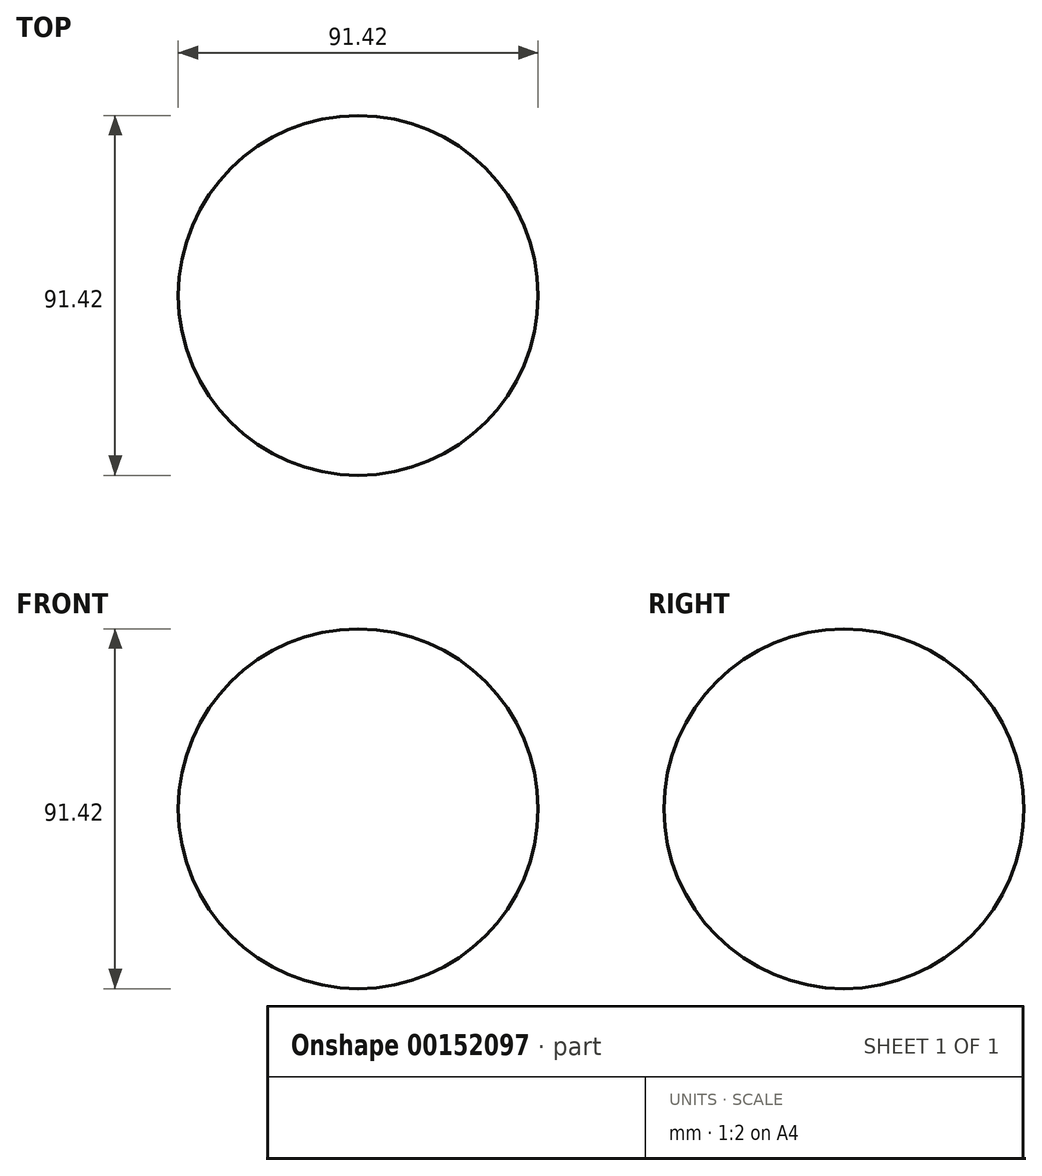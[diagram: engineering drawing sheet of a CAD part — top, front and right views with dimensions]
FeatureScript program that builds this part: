
annotation { "Feature Type Name" : "Feature", "Feature Type Description" : "" }
export const myFeature = defineFeature(function(context is Context, id is Id, definition is map)
    precondition{}
    {
        {
            var Q0;
            Q0=qCreatedBy(makeId("Top.planeOp"),FACE);
            var sketch = newSketch(context, id + "F0", { "sketchPlane" : qUnion([Q0])});
            skLineSegment(sketch, "E0", {"start": v(0, 0) * mm, "end": v(0, 143.05) * mm, "construction": true});
            skLineSegment(sketch, "E1", {"start": v(0, 0) * mm, "end": v(0, -143.05) * mm, "construction": true});
            skArc(sketch, "E2", {"start": v(0, -45.71) * mm, "mid": v(45.71, 0) * mm, "end": v(0, 45.71) * mm});
            skLineSegment(sketch, "E3", {"start": v(0, -45.71) * mm, "end": v(0, 45.71) * mm});
            skSolve(sketch);
        }
        {
            var Q0;
            Q0=makeQuery(id+"F0.imprint","IMPRINT",FACE,{"disambiguationData":[TD([[makeQuery(id+"F0.imprint","IMPRINT",EDGE,{"derivedFrom":sQuery(id+"F0.wireOp",EDGE,"E2")}),1.0]])]});
            var Q1;
            Q1=sQuery(id+"F0.wireOp",EDGE,"E1");
            revolve(context, id + "F1", {"entities" : qUnion([Q0]), "axis" : qUnion([Q1]), "revolveType" : RevolveType.FULL});
        }
    });
